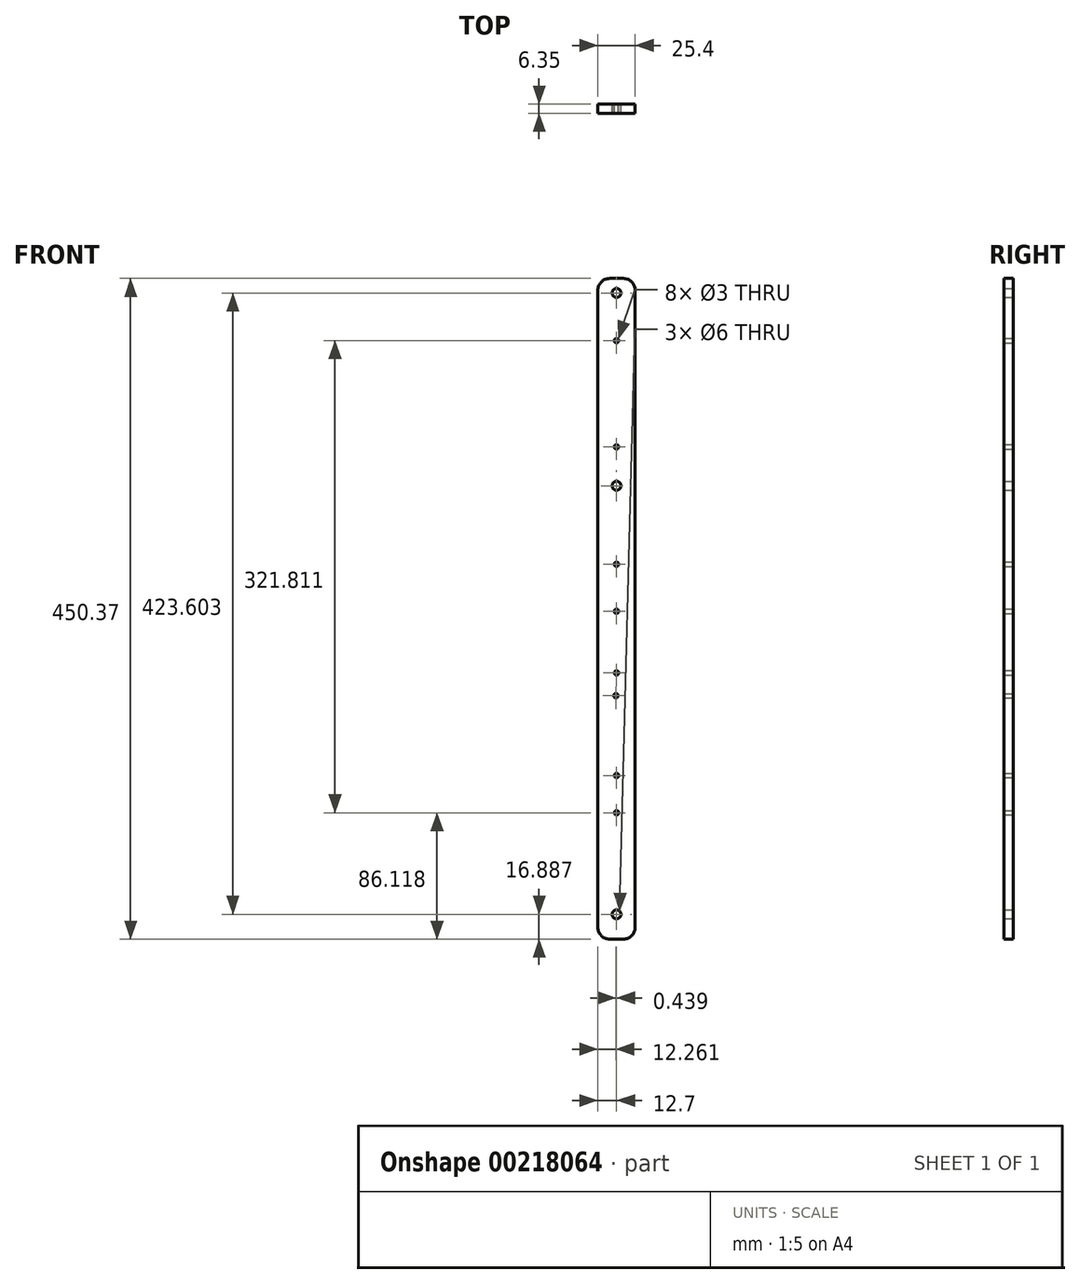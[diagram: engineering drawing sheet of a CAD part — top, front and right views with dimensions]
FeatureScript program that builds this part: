
annotation { "Feature Type Name" : "Feature", "Feature Type Description" : "" }
export const myFeature = defineFeature(function(context is Context, id is Id, definition is map)
    precondition{}
    {
        {
            var Q0;
            Q0=qCreatedBy(makeId("Front.planeOp"),FACE);
            var sketch = newSketch(context, id + "F0", { "sketchPlane" : qUnion([Q0])});
            skCircle(sketch, "E0", {"center": v(0, -85.45) * mm, "radius": 1.5 * mm});
            skCircle(sketch, "E1", {"center": v(-0.44, -31.05) * mm, "radius": 1.5 * mm});
            skCircle(sketch, "E2", {"center": v(0, 26.55) * mm, "radius": 1.5 * mm});
            skLineSegment(sketch, "E3.top", {"start": v(-4.69, -196.97) * mm, "end": v(4.69, -196.97) * mm});
            skLineSegment(sketch, "E3.left", {"start": v(-12.7, 245.38) * mm, "end": v(-12.7, -188.95) * mm});
            skLineSegment(sketch, "E3.right", {"start": v(12.7, 245.38) * mm, "end": v(12.7, -188.95) * mm});
            skPoint(sketch, "E4.visualSharp", {"position": v(12.7, 256.22) * mm});
            skPoint(sketch, "E5.visualSharp", {"position": v(12.7, -196.97) * mm});
            skArc(sketch, "E5.filletArc", {"start": v(4.69, -196.97) * mm, "mid": v(10.35, -194.62) * mm, "end": v(12.7, -188.95) * mm});
            skPoint(sketch, "E6.visualSharp", {"position": v(-12.7, -196.97) * mm});
            skArc(sketch, "E6.filletArc", {"start": v(-12.7, -188.95) * mm, "mid": v(-10.35, -194.62) * mm, "end": v(-4.69, -196.97) * mm});
            skCircle(sketch, "E7", {"center": v(0, 58.56) * mm, "radius": 1.5 * mm});
            skLineSegment(sketch, "E8", {"start": v(0, 26.55) * mm, "end": v(0, 99.81) * mm, "construction": true});
            skLineSegment(sketch, "E9", {"start": v(0, 99.81) * mm, "end": v(0, -85.45) * mm, "construction": true});
            skLineSegment(sketch, "E10", {"start": v(0, -85.45) * mm, "end": v(0, -201.73) * mm, "construction": true});
            skCircle(sketch, "E11", {"center": v(0, 243.52) * mm, "radius": 3 * mm});
            skCircle(sketch, "E12", {"center": v(0, -110.85) * mm, "radius": 1.5 * mm});
            skCircle(sketch, "E13", {"center": v(0, -15.45) * mm, "radius": 1.5 * mm});
            skLineSegment(sketch, "E14", {"start": v(0, 58.56) * mm, "end": v(0, 424.12) * mm});
            skCircle(sketch, "E15", {"center": v(0, 210.96) * mm, "radius": 1.5 * mm});
            skCircle(sketch, "E16", {"center": v(0, 138.56) * mm, "radius": 1.5 * mm});
            skLineSegment(sketch, "E17", {"start": v(12.7, 28.22) * mm, "end": v(-12.7, 28.22) * mm, "construction": true});
            skArc(sketch, "E18.MirrorCS", {"start": v(-12.7, 245.38) * mm, "mid": v(-10.35, 251.05) * mm, "end": v(-4.69, 253.4) * mm});
            skArc(sketch, "E19.MirrorCS", {"start": v(4.69, 253.4) * mm, "mid": v(10.35, 251.05) * mm, "end": v(12.7, 245.38) * mm});
            skLineSegment(sketch, "E20.MirrorCS", {"start": v(-4.69, 253.4) * mm, "end": v(4.69, 253.4) * mm});
            skPoint(sketch, "E21.end.orphan", {"position": v(-12.7, 253.51) * mm});
            skPoint(sketch, "E22.orphan", {"position": v(-12.7, 249.87) * mm});
            skPoint(sketch, "E23.orphan", {"position": v(-7.5, 253.51) * mm});
            skPoint(sketch, "E24.end.orphan", {"position": v(12.7, 253.51) * mm});
            skPoint(sketch, "E24.start.orphan", {"position": v(12.7, 251.2) * mm});
            skPoint(sketch, "E25.start.orphan", {"position": v(7.5, 253.51) * mm});
            skCircle(sketch, "E26", {"center": v(0, -180.08) * mm, "radius": 3 * mm});
            skCircle(sketch, "E27", {"center": v(0, 112.09) * mm, "radius": 3 * mm});
            skSolve(sketch);
        }
        {
            var Q0;
            Q0=makeQuery(id+"F0.imprint","IMPRINT",FACE,{"disambiguationData":[TD([[makeQuery(id+"F0.imprint","IMPRINT",EDGE,{"derivedFrom":sQuery(id+"F0.wireOp",EDGE,"E0")}),-1.0]])]});
            extrude(context, id + "F1", {"entities" : qUnion([Q0]), "depth" : 6.35 * mm});
        }
    });
